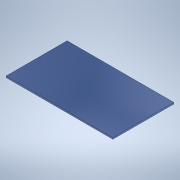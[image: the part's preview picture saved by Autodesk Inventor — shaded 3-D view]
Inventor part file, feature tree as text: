
AUTODESK INVENTOR PART (.ipt)
format: ipt  version: 2020 (Build 240168000, 168)  size: 95,744 bytes
history: native  units: in
note: dims shown in document units (in); Inventor stores cm internally (conversion verified against a paired STEP export)
features: extrude x1, sketch x1
ambient origin geometry x8: Origin, YZ Plane, XZ Plane, XY Plane, X Axis, Y Axis, Z Axis, Center Point
bodies: Solid1 (feature_tree)
feature tree (2):
  extrude  "Extrusion1"  Depth=8.0in
  sketch  "Sketch1"  dims[d0=14.0in d1=8.0in d2=0.1875in d3=0.0in]
